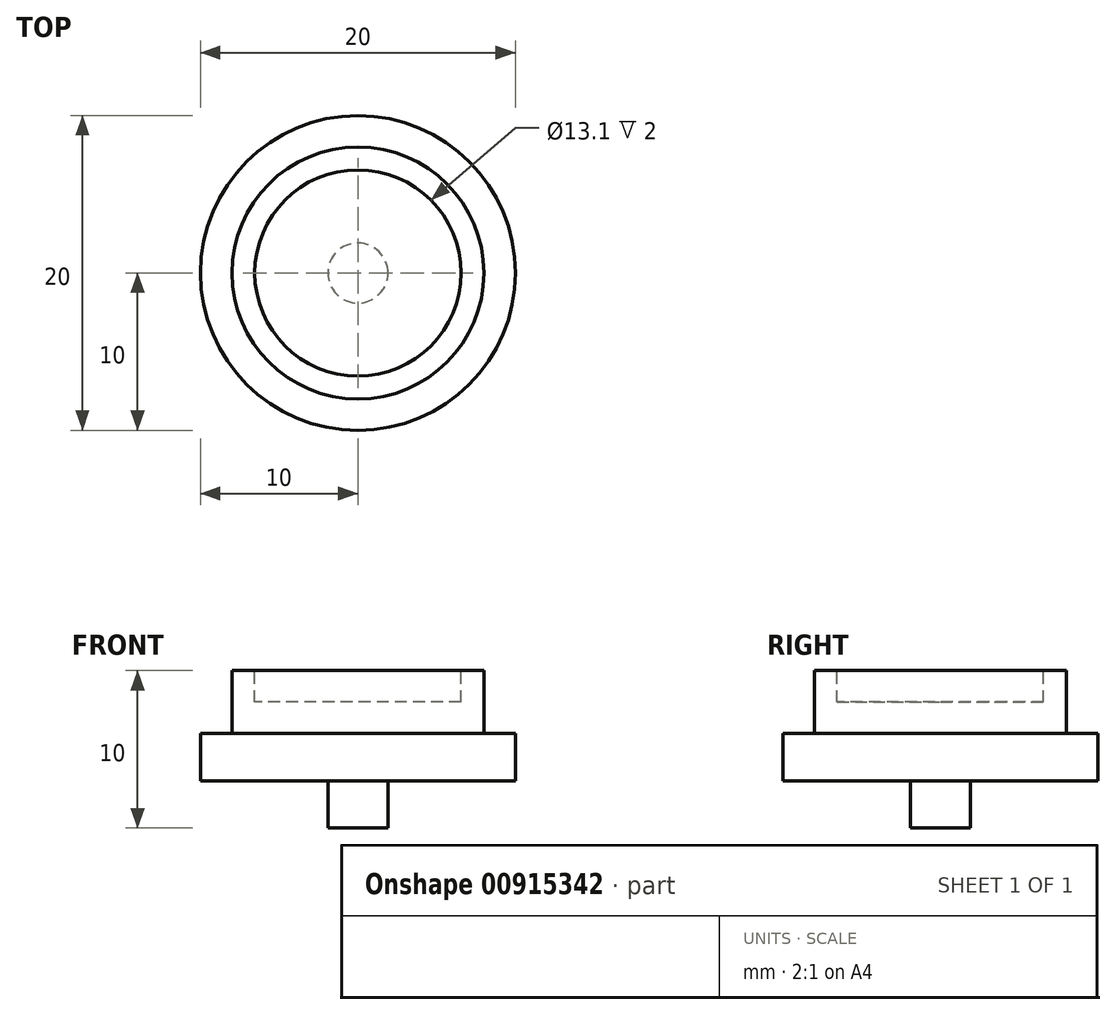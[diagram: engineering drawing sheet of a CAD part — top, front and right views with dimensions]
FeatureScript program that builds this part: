
annotation { "Feature Type Name" : "Feature", "Feature Type Description" : "" }
export const myFeature = defineFeature(function(context is Context, id is Id, definition is map)
    precondition{}
    {
        {
            var Q0;
            Q0=qCreatedBy(makeId("Top.planeOp"),FACE);
            var sketch = newSketch(context, id + "F0", { "sketchPlane" : qUnion([Q0])});
            skCircle(sketch, "E0", {"center": v(0, 0) * mm, "radius": 10 * mm});
            skSolve(sketch);
        }
        {
            var Q0;
            Q0=makeQuery(id+"F0.imprint","IMPRINT",FACE,{"disambiguationData":[TD([[makeQuery(id+"F0.imprint","IMPRINT",EDGE,{"derivedFrom":sQuery(id+"F0.wireOp",EDGE,"E0")}),1.0]])]});
            extrude(context, id + "F1", {"entities" : qUnion([Q0]), "depth" : 3 * mm, "offsetDistance" : 25 * mm});
        }
        {
            var Q0;
            Q0=makeQuery(id+"F1.opExtrude","CAP_FACE",FACE,{"disambiguationData":[OSD([sQuery(id+"F0.wireOp",EDGE,"E0")])],"isStart":false});
            var sketch = newSketch(context, id + "F2", { "sketchPlane" : qUnion([Q0])});
            skCircle(sketch, "E1", {"center": v(0, 0) * mm, "radius": 8 * mm});
            skSolve(sketch);
        }
        {
            var Q0;
            Q0=makeQuery(id+"F2.imprint","IMPRINT",FACE,{"disambiguationData":[TD([[makeQuery(id+"F2.imprint","IMPRINT",EDGE,{"derivedFrom":sQuery(id+"F2.wireOp",EDGE,"E1")}),1.0]])]});
            extrude(context, id + "F3", {"entities" : qUnion([Q0]), "operationType" : NewBodyOperationType.ADD, "depth" : 4 * mm, "offsetDistance" : 25 * mm});
        }
        {
            var Q0;
            Q0=makeQuery(id+"F1.opExtrude","CAP_FACE",FACE,{"disambiguationData":[OSD([sQuery(id+"F0.wireOp",EDGE,"E0")])],"isStart":true});
            var sketch = newSketch(context, id + "F4", { "sketchPlane" : qUnion([Q0])});
            skCircle(sketch, "E2", {"center": v(0, 0) * mm, "radius": 1.9 * mm});
            skSolve(sketch);
        }
        {
            var Q0;
            Q0 = qSketchRegion(id + "F4", true);
            extrude(context, id + "F5", {"entities" : qUnion([Q0]), "operationType" : NewBodyOperationType.ADD, "depth" : 3 * mm, "offsetDistance" : 25 * mm});
        }
        {
            var Q0;
            Q0=makeQuery(id+"F3.opExtrude","CAP_FACE",FACE,{"disambiguationData":[OSD([sQuery(id+"F2.wireOp",EDGE,"E1")])],"isStart":false});
            var sketch = newSketch(context, id + "F6", { "sketchPlane" : qUnion([Q0])});
            skCircle(sketch, "E3", {"center": v(0, 0) * mm, "radius": 6.55 * mm});
            skSolve(sketch);
        }
        {
            var Q0;
            Q0 = qSketchRegion(id + "F6", true);
            extrude(context, id + "F7", {"entities" : qUnion([Q0]), "operationType" : NewBodyOperationType.REMOVE, "oppositeDirection" : true, "depth" : 2 * mm, "offsetDistance" : 25 * mm});
        }
    });
